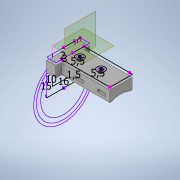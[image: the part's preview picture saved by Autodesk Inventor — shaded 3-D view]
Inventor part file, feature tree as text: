
AUTODESK INVENTOR PART (.ipt)
format: ipt  version: 2021.1 (Build 251245010, 245A)  size: 230,400 bytes
history: native  units: in
note: dims shown in document units (in); Inventor stores cm internally (conversion verified against a paired STEP export)
features: extrude x9, sketch x3, plane x2, fillet x1
ambient origin geometry x8: Origin, YZ Plane, XZ Plane, XY Plane, X Axis, Y Axis, Z Axis, Center Point
bodies: Solid1 (feature_tree)
feature tree (15):
  plane  "Arbeitsebene1"
  sketch  "Skizze1"  dims[d0=0.2165in d1=0.2165in]
  extrude  "Extrusion1"  Depth=0.2165in
  plane  "Arbeitsebene2"
  sketch  "Skizze2"  dims[d2=0.3937in d3=0.0in d4=0.5906in]
  extrude  "Extrusion2"  Depth=0.3937in
  extrude  "Extrusion3"  Depth=0.3937in
  extrude  "Extrusion4"  Depth=0.0197in
  extrude  "Extrusion5"  Depth=0.3937in TaperAngle=0.0deg
  extrude  "Extrusion6"  Depth=0.0197in TaperAngle=0.0deg
  extrude  "Extrusion7"  Depth=0.0197in
  extrude  "Extrusion8"  Depth=0.0197in
  extrude  "Extrusion9"  Depth=0.0197in TaperAngle=0.0deg
  fillet  "Rundung1"  Radius=1.2795in
  sketch  "Skizze4"  dims[d5=0.6299in d6=0.3937in d7=0.0591in d8=0.3937in d9=0.0in d12=0.1969in d13=0.0in d14=0.1181in d15=0.0787in d16=1.4961in d17=0.0in d18=1.2795in d19=0.0in d20=0.8681in d21=0.0in d22=0.6516in d23=0.0in d24=0.6516in d25=0.0in d26=0.0787in d27=0.0in d28=0.0197in d29=0.2205in d30=0.2205in]
